# Revit family: Legrand-Ups-Keor_HP-100_800kVA
name_source: partatom
category: Installations électriques
revit_build: Autodesk Revit 2018 (Build: 20170223_1515(x64)
units: mm (PartAtom-declared; Revit-internal decimal feet)

## family parameters
Basée sur le plan de construction = Non
Conserver l'orientation des annotations = Non
Cote de connecteur circulaire = Utiliser le diamètre
Couper avec des vides une fois chargée = Non
Numéro OmniClass = 23.80.10.17.34
Partagée = Non
Point de calcul de pièce = Non
Titre OmniClass = Static Uninterruptible Power Supplies
Toujours verticalement = Oui
Type d'élément = Normal

## types (30) — shared parameters
Conductors = Cables
Fabricant = LEGRAND
Front Clearance = 1000 mm  [stored 3.28084 ft]
General Conditions of Use = https://export.legrand.com
Humidity = 0-95% not condensing
Installation type = On the floor
Modèle = KEOR HP
Operating altitude = up to 1000 m altitude without derating
Operating temperature = from 0°C to +40°C
Side Clearance = 50 mm  [stored 0.164042 ft]
URL = https://ups.legrand.com
Visibilità aree d'installazione = Oui
zero-valued in all types: Back Clearance

## per-type parameters (varying)
| type | Active power of use | Additional Cabinet | Cabinet Depth | Cabinet Height | Cabinet Width | Connection constraint | Connection constraint (signal) | Frequency of use | Input / Output phase configuration | Installation space | Left Width | Max sound pressure level | Nominal Power | Output Voltage | Output power factor | Right Width | UPS Only | Weight |
| 960430 | 90 kW | Non | 825 mm  [stored 2.70669 ft] | 1670 mm | 815 mm  [stored 2.67388 ft] | Ahead and bottom | Ahead and above/bottom | 50 Hz or 60 Hz selectable | 3ph+PE/3ph+N+PE | 1.12 m³ | 408 mm | < 60 dB at 1m | 100 kVA | 380,400,415 Vac | 0.9 | 408 mm | Oui | 625.0 kg |
| 960431 | 113 kW | Non | 825 mm  [stored 2.70669 ft] | 1670 mm | 815 mm  [stored 2.67388 ft] | Ahead and bottom | Ahead and above/bottom | 50 Hz or 60 Hz selectable | 3ph+PE/3ph+N+PE | 1.12 m³ | 408 mm | < 60 dB at 1m | 125 kVA | 380,400,415 Vac | 0.9 | 408 mm | Oui | 660.0 kg |
| 960432 | 144 kW | Non | 825 mm  [stored 2.70669 ft] | 1670 mm | 815 mm  [stored 2.67388 ft] | Ahead and bottom | Ahead and above/bottom | 50 Hz or 60 Hz selectable | 3ph+PE/3ph+N+PE | 1.12 m³ | 408 mm | < 60 dB at 1m | 160 kVA | 380,400,415 Vac | 0.9 | 408 mm | Oui | 715.0 kg |
| 960433 | 180 kW | Non | 870 mm  [stored 2.85433 ft] | 1905 mm  [stored 6.25 ft] | 1220 mm  [stored 4.00262 ft] | Ahead and bottom | Ahead and above/bottom | 50 Hz or 60 Hz selectable | 3ph+PE/3ph+N+PE | 2 m³ | 813 mm | < 62 dB at 1m | 200 kVA | 380,400,415 Vac | 0.9 | 408 mm | Oui | 970.0 kg |
| 960434 | 225 kW | Non | 870 mm  [stored 2.85433 ft] | 1905 mm  [stored 6.25 ft] | 1220 mm  [stored 4.00262 ft] | Ahead and bottom | Ahead and above/bottom | 50 Hz or 60 Hz selectable | 3ph+PE/3ph+N+PE | 2 m³ | 813 mm | < 62 dB at 1m | 250 kVA | 380,400,415 Vac | 0.9 | 408 mm | Oui | 1090.0 kg |
| 960435 | 270 kW | Non | 870 mm  [stored 2.85433 ft] | 1905 mm  [stored 6.25 ft] | 1220 mm  [stored 4.00262 ft] | Ahead and bottom | Ahead and above/bottom | 50 Hz or 60 Hz selectable | 3ph+PE/3ph+N+PE | 2 m³ | 813 mm | < 62 dB at 1m | 300 kVA | 380,400,415 Vac | 0.9 | 408 mm | Oui | 1170.0 kg |
| 960436 | 360 kW | Non | 965 mm  [stored 3.16601 ft] | 1920 mm  [stored 6.29921 ft] | 1990 mm  [stored 6.52887 ft] | Ahead and bottom | Ahead and above/bottom | 50 Hz or 60 Hz selectable | 3ph+PE/3ph+N+PE | 3.6 m³ | 408 mm | < 62 dB at 1m | 400 kVA | 380,400,415 Vac | 0.9 | 1583 mm | Oui | 1820.0 kg |
| 960437 | 450 kW | Non | 965 mm  [stored 3.16601 ft] | 2020 mm  [stored 6.6273 ft] | 2440 mm  [stored 8.00525 ft] | Ahead and bottom | Ahead and above/bottom | 50 Hz or 60 Hz selectable | 3ph+PE/3ph+N+PE | 4.7 m³ | 408 mm | < 62 dB at 1m | 500 kVA | 380,400,415 Vac | 0.9 | 2033 mm | Oui | 2220.0 kg |
| 960438 | 540 kW | Non | 965 mm  [stored 3.16601 ft] | 2020 mm  [stored 6.6273 ft] | 2440 mm  [stored 8.00525 ft] | Ahead and bottom | Ahead and above/bottom | 50 Hz or 60 Hz selectable | 3ph+PE/3ph+N+PE | 4.7 m³ | 408 mm | < 62 dB at 1m | 600 kVA | 380,400,415 Vac | 0.9 | 2033 mm | Oui | 2400.0 kg |
| 960439 | 720 kW | Non | 965 mm  [stored 3.16601 ft] | 1920 mm  [stored 6.29921 ft] | 3640 mm | Ahead and bottom | Ahead and above/bottom | 50 Hz or 60 Hz selectable | 3ph+PE/3ph+N+PE | 6.7 m³ | 793 mm | < 62 dB at 1m | 800 kVA | 380,400,415 Vac | 0.9 | 2848 mm | Oui | 3600.0 kg |
| 960440 | 0 kW | Oui | 950 mm  [stored 3.1168 ft] | 1920 mm  [stored 6.29921 ft] | 550 mm | Ahead and above |  |  |  | 1 m³ | 275 mm |  | 0 kVA |  | 0 | 275 mm | Non | 175.0 kg |
| 960441 | 0 kW | Oui | 950 mm  [stored 3.1168 ft] | 2020 mm  [stored 6.6273 ft] | 570 mm  [stored 1.87008 ft] | Ahead and above |  |  |  | 1.09 m³ | 285 mm  [stored 0.935039 ft] |  | 0 kVA |  | 0 | 285 mm  [stored 0.935039 ft] | Non | 195.0 kg |
| 960442 | 0 kW | Oui | 950 mm  [stored 3.1168 ft] | 2020 mm  [stored 6.6273 ft] | 570 mm  [stored 1.87008 ft] | Ahead and above |  |  |  | 1.09 m³ | 285 mm  [stored 0.935039 ft] |  | 0 kVA |  | 0 | 285 mm  [stored 0.935039 ft] | Non | 195.0 kg |
| 960443 | 0 kW | Oui | 950 mm  [stored 3.1168 ft] | 1920 mm  [stored 6.29921 ft] | 570 mm  [stored 1.87008 ft] | Ahead and above |  |  |  | 1 m³ | 285 mm  [stored 0.935039 ft] |  | 0 kVA |  | 0 | 285 mm  [stored 0.935039 ft] | Non | 225.0 kg |
| 960454 | 0 kW | Oui | 825 mm  [stored 2.70669 ft] | 1670 mm | 490 mm  [stored 1.60761 ft] | Ahead and above |  |  |  | 1 m³ | 245 mm  [stored 0.803806 ft] |  | 0 kVA |  | 0 | 245 mm  [stored 0.803806 ft] | Non | 120.0 kg |
| 960455 | 0 kW | Oui | 855 mm  [stored 2.80512 ft] | 1950 mm  [stored 6.39764 ft] | 550 mm | Ahead and above |  |  |  | 0.91 m³ | 275 mm |  | 0 kVA |  | 0 | 275 mm | Non | 120.0 kg |
| 960456 | 0 kW | Oui | 950 mm  [stored 3.1168 ft] | 1920 mm  [stored 6.29921 ft] | 550 mm | Ahead and above |  |  |  | 1 m³ | 275 mm |  | 0 kVA |  | 0 | 275 mm | Non | 190.0 kg |
| 960457 | 0 kW | Oui | 950 mm  [stored 3.1168 ft] | 2020 mm  [stored 6.6273 ft] | 550 mm | Ahead and above |  |  |  | 1 m³ | 275 mm |  | 0 kVA |  | 0 | 275 mm | Non | 240.0 kg |
| 960458 | 0 kW | Oui | 950 mm  [stored 3.1168 ft] | 2020 mm  [stored 6.6273 ft] | 550 mm | Ahead and above |  |  |  | 1 m³ | 275 mm |  | 0 kVA |  | 0 | 275 mm | Non | 260.0 kg |
| 960459 | 0 kW | Oui | 950 mm  [stored 3.1168 ft] | 1920 mm  [stored 6.29921 ft] | 770 mm  [stored 2.52625 ft] | Ahead and above |  |  |  | 1.4 m³ | 385 mm  [stored 1.26312 ft] |  | 0 kVA |  | 0 | 385 mm  [stored 1.26312 ft] | Non | 300.0 kg |
| 960444 | 0 kW | Oui | 825 mm  [stored 2.70669 ft] | 1670 mm | 490 mm  [stored 1.60761 ft] | Ahead and above |  |  |  | 0.67 m³ | 245 mm  [stored 0.803806 ft] |  | 0 kVA |  | 0 | 245 mm  [stored 0.803806 ft] | Non | 468.0 kg |
| 960445 | 0 kW | Oui | 825 mm  [stored 2.70669 ft] | 1670 mm | 490 mm  [stored 1.60761 ft] | Ahead and above |  |  |  | 0.67 m³ | 245 mm  [stored 0.803806 ft] |  | 0 kVA |  | 0 | 245 mm  [stored 0.803806 ft] | Non | 488.0 kg |
| 960446 | 0 kW | Oui | 825 mm  [stored 2.70669 ft] | 1670 mm | 490 mm  [stored 1.60761 ft] | Ahead and above |  |  |  | 0.67 m³ | 245 mm  [stored 0.803806 ft] |  | 0 kVA |  | 0 | 245 mm  [stored 0.803806 ft] | Non | 508.0 kg |
| 960447 | 0 kW | Oui | 855 mm  [stored 2.80512 ft] | 1950 mm  [stored 6.39764 ft] | 550 mm | Ahead and above |  |  |  | 0.91 m³ | 275 mm |  | 0 kVA |  | 0 | 275 mm | Non | 570.0 kg |
| 960448 | 0 kW | Oui | 855 mm  [stored 2.80512 ft] | 1950 mm  [stored 6.39764 ft] | 550 mm | Ahead and above |  |  |  | 0.91 m³ | 275 mm |  | 0 kVA |  | 0 | 275 mm | Non | 725.0 kg |
| 960449 | 0 kW | Oui | 855 mm  [stored 2.80512 ft] | 1950 mm  [stored 6.39764 ft] | 550 mm | Ahead and above |  |  |  | 0.91 m³ | 275 mm |  | 0 kVA |  | 0 | 275 mm | Non | 1005.0 kg |
| 960450 | 0 kW | Oui | 950 mm  [stored 3.1168 ft] | 1920 mm  [stored 6.29921 ft] | 550 mm | Ahead and above |  |  |  | 1 m³ | 275 mm |  | 0 kVA |  | 0 | 275 mm | Non | 1150.0 kg |
| 960451 | 0 kW | Oui | 950 mm  [stored 3.1168 ft] | 2020 mm  [stored 6.6273 ft] | 550 mm | Ahead and above |  |  |  | 1 m³ | 275 mm |  | 0 kVA |  | 0 | 275 mm | Non | 1250.0 kg |
| 960452 | 0 kW | Oui | 950 mm  [stored 3.1168 ft] | 2020 mm  [stored 6.6273 ft] | 550 mm | Ahead and above |  |  |  | 1 m³ | 275 mm |  | 0 kVA |  | 0 | 275 mm | Non | 1450.0 kg |
| 960453 | 0 kW | Oui | 950 mm  [stored 3.1168 ft] | 1920 mm  [stored 6.29921 ft] | 1200 mm  [stored 3.93701 ft] | Ahead and above |  |  |  | 2.1 m³ | 600 mm |  | 0 kVA |  | 0 | 600 mm | Non | 1600.0 kg |

note: [stored X ft] marks values corroborated as IEEE doubles in the binary element streams (Revit-internal decimal feet)
